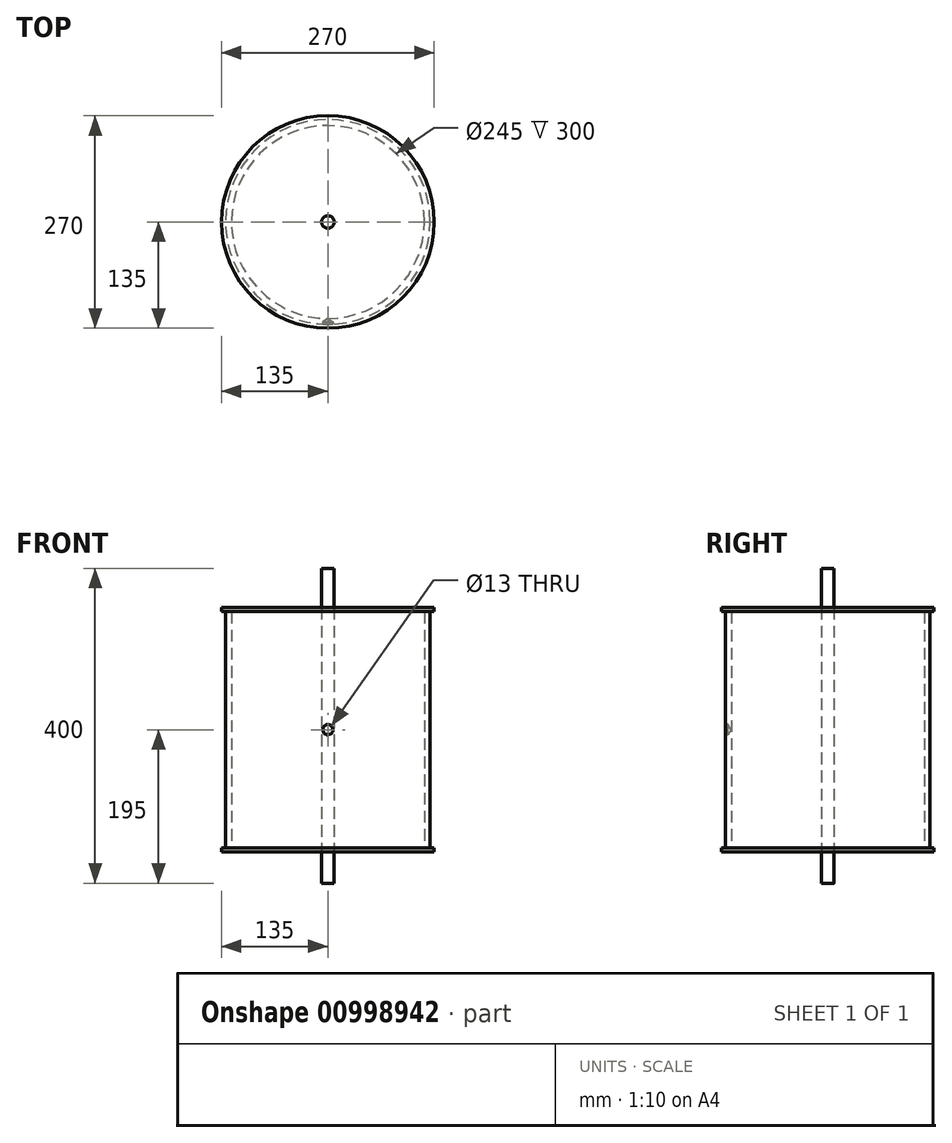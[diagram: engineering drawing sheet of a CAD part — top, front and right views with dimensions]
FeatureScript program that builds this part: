
annotation { "Feature Type Name" : "Feature", "Feature Type Description" : "" }
export const myFeature = defineFeature(function(context is Context, id is Id, definition is map)
    precondition{}
    {
        {
            var Q0;
            Q0=qCreatedBy(makeId("Top.planeOp"),FACE);
            var sketch = newSketch(context, id + "F0", { "sketchPlane" : qUnion([Q0])});
            skCircle(sketch, "E0", {"center": v(0, 0) * mm, "radius": 135 * mm});
            skCircle(sketch, "E1", {"center": v(0, 0) * mm, "radius": 122.5 * mm});
            skCircle(sketch, "E2", {"center": v(0, 0) * mm, "radius": 130 * mm});
            skSolve(sketch);
        }
        {
            var Q0;
            Q0=makeQuery(id+"F0.imprint","IMPRINT",FACE,{"disambiguationData":[TD([[makeQuery(id+"F0.imprint","IMPRINT",EDGE,{"derivedFrom":sQuery(id+"F0.wireOp",EDGE,"E1")}),-1.0]])]});
            extrude(context, id + "F1", {"entities" : qUnion([Q0]), "depth" : 150 * mm, "offsetDistance" : 25.4 * mm});
        }
        {
            var Q0;
            Q0=makeQuery(id+"F0.imprint","IMPRINT",FACE,{"disambiguationData":[TD([[makeQuery(id+"F0.imprint","IMPRINT",EDGE,{"derivedFrom":sQuery(id+"F0.wireOp",EDGE,"E1")}),1.0]])]});
            cPlane(context, id + "F2", {"entities" : qUnion([Q0]), "cplaneType" : CPlaneType.OFFSET, "offset" : 150 * mm, "width" : 152.4 * mm, "height" : 152.4 * mm});
        }
        {
            var Q0;
            Q0=makeQuery(id+"F0.imprint","IMPRINT",FACE,{"disambiguationData":[TD([[makeQuery(id+"F0.imprint","IMPRINT",EDGE,{"derivedFrom":sQuery(id+"F0.wireOp",EDGE,"E1")}),1.0]])]});
            var Q1;
            Q1=makeQuery(id+"F0.imprint","IMPRINT",FACE,{"disambiguationData":[TD([[makeQuery(id+"F0.imprint","IMPRINT",EDGE,{"derivedFrom":sQuery(id+"F0.wireOp",EDGE,"E1")}),-1.0]])]});
            var Q2;
            Q2=makeQuery(id+"F0.imprint","IMPRINT",FACE,{"disambiguationData":[TD([[makeQuery(id+"F0.imprint","IMPRINT",EDGE,{"derivedFrom":sQuery(id+"F0.wireOp",EDGE,"E0")}),1.0]])]});
            extrude(context, id + "F3", {"entities" : qUnion([Q0, Q1, Q2]), "oppositeDirection" : true, "depth" : 5 * mm, "offsetDistance" : 25.4 * mm});
        }
        {
            var Q0;
            Q0=makeQuery(id+"F1.opExtrude","SWEPT_BODY",BODY,{"disambiguationData":[OSD([sQuery(id+"F0.wireOp",EDGE,"E1"),sQuery(id+"F0.wireOp",EDGE,"E2")])]});
            var Q1;
            Q1=makeQuery(id+"F3.opExtrude","SWEPT_BODY",BODY,{"disambiguationData":[OSD([sQuery(id+"F0.wireOp",EDGE,"E0")])]});
            var Q2;
            Q2=qCreatedBy(id+"F2.planeOp",FACE);
            mirror(context, id + "F4", {"operationType" : NewBodyOperationType.ADD, "entities" : qUnion([Q0, Q1]), "mirrorPlane" : qUnion([Q2])});
        }
        {
            var Q0;
            Q0=qCreatedBy(makeId("Front.planeOp"),FACE);
            cPlane(context, id + "F5", {"entities" : qUnion([Q0]), "cplaneType" : CPlaneType.OFFSET, "offset" : 130 * mm, "width" : 152.4 * mm, "height" : 152.4 * mm});
        }
        {
            var Q0;
            Q0=qCreatedBy(id+"F5.planeOp",FACE);
            var sketch = newSketch(context, id + "F6", { "sketchPlane" : qUnion([Q0])});
            skLineSegment(sketch, "E3", {"start": v(0, 0) * mm, "end": v(0, 150) * mm});
            skPoint(sketch, "E4", {"position": v(0, 150) * mm});
            skSolve(sketch);
        }
        {
            var Q0;
            Q0=sQuery(id+"F6.wireOp",VERTEX,"E4");
            var Q1;
            Q1=makeQuery(id+"F1.opExtrude","SWEPT_BODY",BODY,{"disambiguationData":[OSD([sQuery(id+"F0.wireOp",EDGE,"E1"),sQuery(id+"F0.wireOp",EDGE,"E2")])]});
            hole(context, id + "F7", {"style" : HoleStyle.SIMPLE, "endStyle" : HoleEndStyle.BLIND, "holeDiameter" : 13 * mm, "majorDiameter" : 6.35 * mm, "holeDepth" : 3.17 * mm, "isTappedThrough" : true, "tappedDepth" : 12.7 * mm, "tapClearance" : 3, "startFromSketch" : true, "locations" : qUnion([Q0]), "scope" : qUnion([Q1])});
        }
        {
            var Q0;
            Q0=makeQuery(id+"F4.opPattern","COPY",FACE,{"derivedFrom":makeQuery(id+"F3.opExtrude","CAP_FACE",FACE,{"disambiguationData":[OSD([sQuery(id+"F0.wireOp",EDGE,"E0")])],"isStart":false}),"instanceName":"1"});
            var sketch = newSketch(context, id + "F8", { "sketchPlane" : qUnion([Q0])});
            skCircle(sketch, "E5", {"center": v(0, 0) * mm, "radius": 7.94 * mm});
            skSolve(sketch);
        }
        {
            var Q0;
            Q0=makeQuery(id+"F8.imprint","IMPRINT",FACE,{"disambiguationData":[TD([[makeQuery(id+"F8.imprint","IMPRINT",EDGE,{"derivedFrom":sQuery(id+"F8.wireOp",EDGE,"E5")}),1.0]])]});
            extrude(context, id + "F9", {"entities" : qUnion([Q0]), "depth" : 50 * mm, "offsetDistance" : 25.4 * mm, "hasSecondDirection" : true, "secondDirectionOppositeDirection" : true, "secondDirectionDepth" : 350 * mm});
        }
    });
